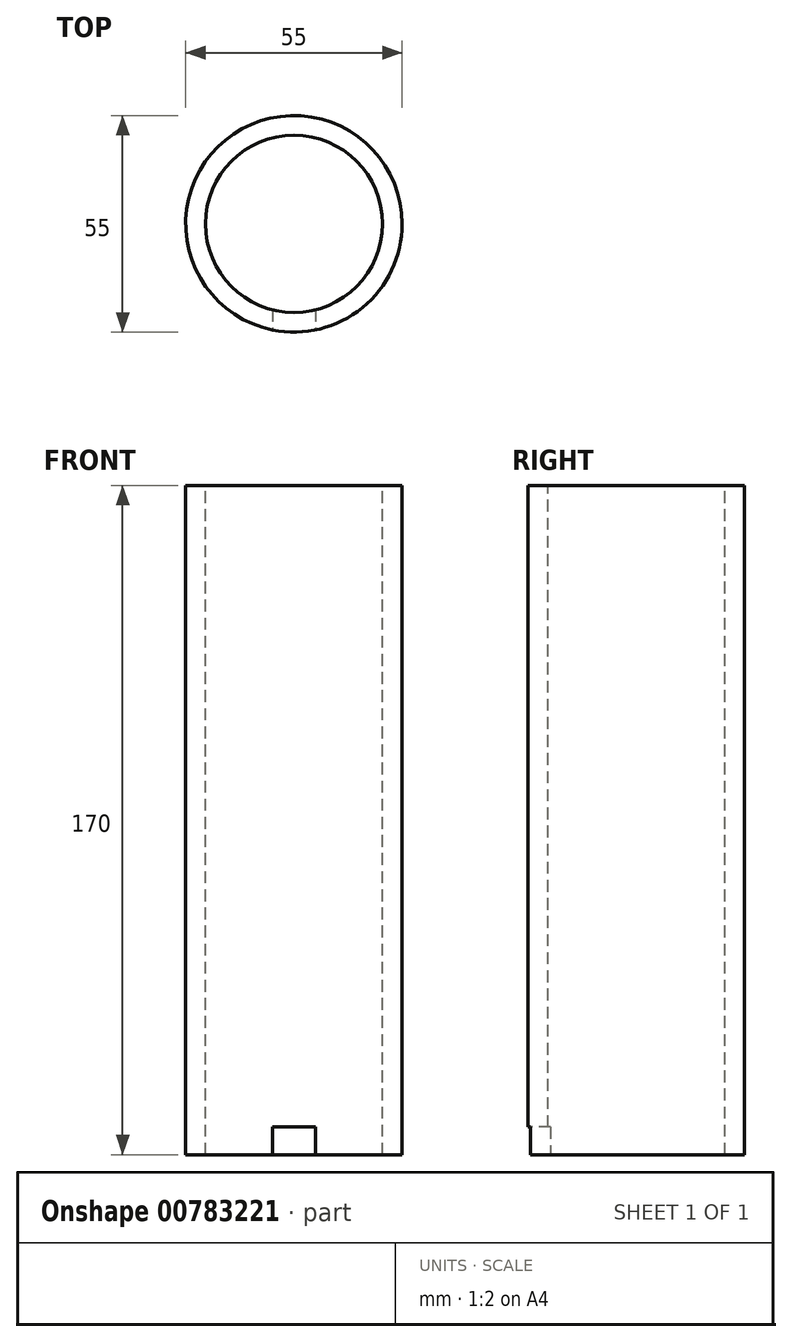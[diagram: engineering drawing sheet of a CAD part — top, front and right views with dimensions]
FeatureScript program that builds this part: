
annotation { "Feature Type Name" : "Feature", "Feature Type Description" : "" }
export const myFeature = defineFeature(function(context is Context, id is Id, definition is map)
    precondition{}
    {
        {
            var Q0;
            Q0=qCreatedBy(makeId("Top.planeOp"),FACE);
            var sketch = newSketch(context, id + "F0", { "sketchPlane" : qUnion([Q0])});
            skLineSegment(sketch, "E0", {"start": v(-25.44, -61.4) * mm, "end": v(24.56, -61.4) * mm});
            skLineSegment(sketch, "E1", {"start": v(24.56, -61.4) * mm, "end": v(59.91, -26.04) * mm});
            skLineSegment(sketch, "E2", {"start": v(59.91, -26.04) * mm, "end": v(59.91, 23.96) * mm});
            skLineSegment(sketch, "E3", {"start": v(59.91, 23.96) * mm, "end": v(24.56, 59.32) * mm});
            skLineSegment(sketch, "E4", {"start": v(24.56, 59.32) * mm, "end": v(-25.44, 59.32) * mm});
            skLineSegment(sketch, "E5", {"start": v(-25.44, 59.32) * mm, "end": v(-60.8, 23.96) * mm});
            skLineSegment(sketch, "E6", {"start": v(-60.8, 23.96) * mm, "end": v(-60.8, -26.04) * mm});
            skLineSegment(sketch, "E7", {"start": v(-60.8, -26.04) * mm, "end": v(-25.44, -61.4) * mm});
            skLineSegment(sketch, "E8.0", {"start": v(54.91, 21.9) * mm, "end": v(22.48, 54.32) * mm});
            skLineSegment(sketch, "E8.1", {"start": v(54.91, -23.97) * mm, "end": v(54.91, 21.9) * mm});
            skLineSegment(sketch, "E8.2", {"start": v(22.48, 54.32) * mm, "end": v(-23.37, 54.32) * mm});
            skLineSegment(sketch, "E8.3", {"start": v(22.48, -56.4) * mm, "end": v(54.91, -23.97) * mm});
            skLineSegment(sketch, "E8.4", {"start": v(-23.37, 54.32) * mm, "end": v(-55.8, 21.9) * mm});
            skLineSegment(sketch, "E8.5", {"start": v(-55.8, 21.9) * mm, "end": v(-55.8, -23.97) * mm});
            skLineSegment(sketch, "E8.6", {"start": v(-55.8, -23.97) * mm, "end": v(-23.37, -56.4) * mm});
            skLineSegment(sketch, "E8.7", {"start": v(-23.37, -56.4) * mm, "end": v(22.48, -56.4) * mm});
            skLineSegment(sketch, "E9.0", {"start": v(-60.8, -26.04) * mm, "end": v(-26.9, -59.93) * mm});
            skLineSegment(sketch, "E9.2", {"start": v(59.91, -23.97) * mm, "end": v(59.91, 23.96) * mm});
            skLineSegment(sketch, "E10.0", {"start": v(49.71, 19.74) * mm, "end": v(20.33, 49.12) * mm});
            skLineSegment(sketch, "E10.1", {"start": v(49.71, -21.81) * mm, "end": v(49.71, 19.74) * mm});
            skLineSegment(sketch, "E10.2", {"start": v(20.33, 49.12) * mm, "end": v(-21.22, 49.12) * mm});
            skLineSegment(sketch, "E10.3", {"start": v(20.33, -51.2) * mm, "end": v(49.71, -21.81) * mm});
            skLineSegment(sketch, "E10.4", {"start": v(-21.22, 49.12) * mm, "end": v(-50.6, 19.74) * mm});
            skLineSegment(sketch, "E10.5", {"start": v(-50.6, 19.74) * mm, "end": v(-50.6, -21.81) * mm});
            skLineSegment(sketch, "E10.6", {"start": v(-50.6, -21.81) * mm, "end": v(-21.22, -51.2) * mm});
            skLineSegment(sketch, "E10.7", {"start": v(-21.22, -51.2) * mm, "end": v(20.33, -51.2) * mm});
            skLineSegment(sketch, "E11", {"start": v(-0.44, 49.12) * mm, "end": v(-0.44, -51.2) * mm});
            skLineSegment(sketch, "E12", {"start": v(-50.6, 0) * mm, "end": v(49.71, -1.04) * mm});
            skSolve(sketch);
        }
        {
            var Q0;
            Q0=makeQuery(id+"F0.imprint","IMPRINT",FACE,{"disambiguationData":[TD([[makeQuery(id+"F0.imprint","IMPRINT",EDGE,{"derivedFrom":sQuery(id+"F0.wireOp",EDGE,"E10.0")}),1.0]])]});
            var sketch = newSketch(context, id + "F1", { "sketchPlane" : qUnion([Q0])});
            skCircle(sketch, "E13", {"center": v(0, 0) * mm, "radius": 27.5 * mm});
            skSolve(sketch);
        }
        {
            var Q0;
            {var subQ0=sQuery(id+"F1.wireOp",EDGE,"E13");var subQ1=sQuery(id+"F0.wireOp",EDGE,"E11");var subQ4=makeQuery(id+"F0.imprint","IMPRINT",EDGE,{"disambiguationData":[TD([[makeQuery(id+"F0.imprint","INTERSECT",VERTEX,{"derivedFrom":[sQuery(id+"F0.wireOp",EDGE,"E10.2"),subQ1]}),-1.0]])],"derivedFrom":subQ1});var subQ5=makeQuery(id+"F1.imprint","INTERSECT",VERTEX,{"derivedFrom":[subQ4,subQ0]});Q0=makeQuery(id+"F1.imprint","IMPRINT",FACE,{"disambiguationData":[TD([[makeQuery(id+"F1.imprint","IMPRINT",EDGE,{"disambiguationData":[TD([[subQ5,1.0]])],"derivedFrom":subQ0}),1.0]])]});}
            var Q1;
            {var subQ0=sQuery(id+"F1.wireOp",EDGE,"E13");var subQ1=sQuery(id+"F0.wireOp",EDGE,"E11");var subQ4=makeQuery(id+"F0.imprint","IMPRINT",EDGE,{"disambiguationData":[TD([[makeQuery(id+"F0.imprint","INTERSECT",VERTEX,{"derivedFrom":[sQuery(id+"F0.wireOp",EDGE,"E10.2"),subQ1]}),-1.0]])],"derivedFrom":subQ1});var subQ5=makeQuery(id+"F1.imprint","INTERSECT",VERTEX,{"derivedFrom":[subQ4,subQ0]});Q1=makeQuery(id+"F1.imprint","IMPRINT",FACE,{"disambiguationData":[TD([[makeQuery(id+"F1.imprint","IMPRINT",EDGE,{"disambiguationData":[TD([[subQ5,-1.0]])],"derivedFrom":subQ0}),1.0]])]});}
            extrude(context, id + "F2", {"entities" : qUnion([Q0, Q1]), "depth" : 170 * mm, "offsetDistance" : 25 * mm});
        }
        {
            var Q0;
            Q0=makeQuery(id+"F2.opExtrude","CAP_FACE",FACE,{"disambiguationData":[OSD([sQuery(id+"F1.wireOp",EDGE,"E13")])],"isStart":false});
            var sketch = newSketch(context, id + "F3", { "sketchPlane" : qUnion([Q0])});
            skCircle(sketch, "E14", {"center": v(0, 0) * mm, "radius": 22.5 * mm});
            skSolve(sketch);
        }
        {
            var Q0;
            Q0=makeQuery(id+"F3.imprint","IMPRINT",FACE,{"disambiguationData":[TD([[makeQuery(id+"F3.imprint","IMPRINT",EDGE,{"derivedFrom":sQuery(id+"F3.wireOp",EDGE,"E14")}),1.0]])]});
            extrude(context, id + "F4", {"entities" : qUnion([Q0]), "operationType" : NewBodyOperationType.REMOVE, "oppositeDirection" : true, "depth" : 170 * mm, "offsetDistance" : 25 * mm});
        }
        {
            var Q0;
            Q0=makeQuery(id+"F2.opExtrude","CAP_FACE",FACE,{"disambiguationData":[OSD([sQuery(id+"F1.wireOp",EDGE,"E13")])],"isStart":true});
            var sketch = newSketch(context, id + "F5", { "sketchPlane" : qUnion([Q0])});
            skLineSegment(sketch, "E15.bottom", {"start": v(0, 0) * mm, "end": v(5.5, 0) * mm});
            skLineSegment(sketch, "E15.top", {"start": v(0, 27.5) * mm, "end": v(5.5, 27.5) * mm});
            skLineSegment(sketch, "E15.right", {"start": v(5.5, 0) * mm, "end": v(5.5, 27.5) * mm});
            skLineSegment(sketch, "E16.bottom", {"start": v(0, 0) * mm, "end": v(-5.5, 0) * mm});
            skLineSegment(sketch, "E16.top", {"start": v(0, 26.94) * mm, "end": v(-5.5, 26.94) * mm});
            skLineSegment(sketch, "E16.right", {"start": v(-5.5, 0) * mm, "end": v(-5.5, 26.94) * mm});
            skSolve(sketch);
        }
        {
            var Q0;
            {var subQ0=makeQuery(id+"F2.opExtrude","CAP_EDGE",EDGE,{"disambiguationData":[OSD([sQuery(id+"F1.wireOp",EDGE,"E13")])],"isStart":true});var subQ2=sQuery(id+"F5.wireOp",EDGE,"E15.right");var subQ3=makeQuery(id+"F5.imprint","INTERSECT",VERTEX,{"derivedFrom":[subQ0,subQ2]});Q0=makeQuery(id+"F5.imprint","IMPRINT",FACE,{"disambiguationData":[TD([[makeQuery(id+"F5.imprint","IMPRINT",EDGE,{"disambiguationData":[TD([[subQ3,1.0]])],"derivedFrom":subQ2}),1.0]])]});}
            extrude(context, id + "F6", {"entities" : qUnion([Q0]), "operationType" : NewBodyOperationType.REMOVE, "oppositeDirection" : true, "depth" : 7 * mm, "offsetDistance" : 25 * mm});
        }
    });
